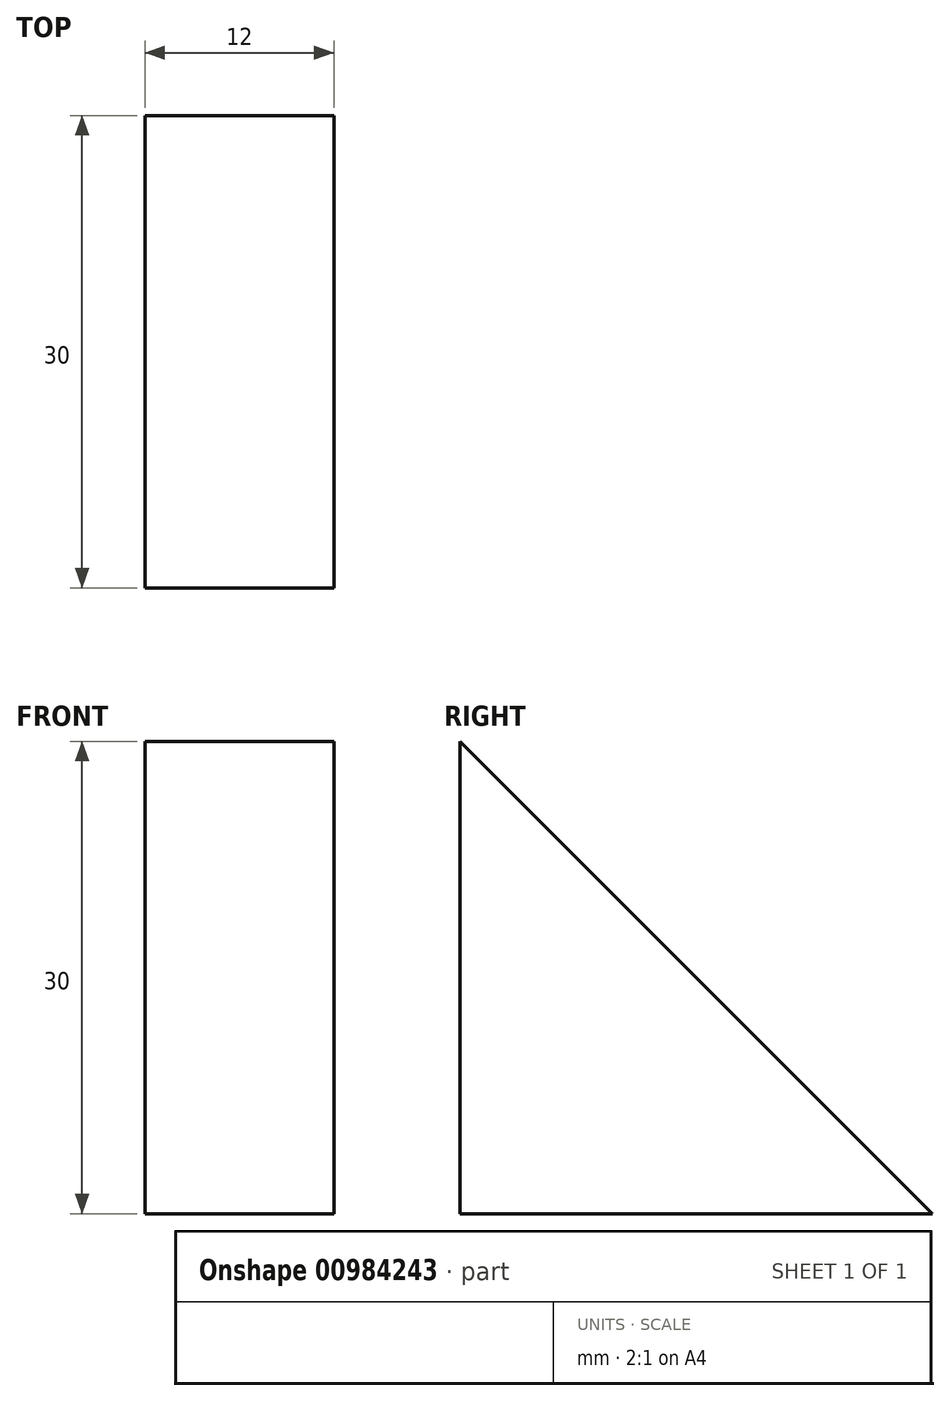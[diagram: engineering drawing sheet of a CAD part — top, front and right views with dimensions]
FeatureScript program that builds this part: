
annotation { "Feature Type Name" : "Feature", "Feature Type Description" : "" }
export const myFeature = defineFeature(function(context is Context, id is Id, definition is map)
    precondition{}
    {
        {
            var Q0;
            Q0=qCreatedBy(makeId("Right.planeOp"),FACE);
            var sketch = newSketch(context, id + "F0", { "sketchPlane" : qUnion([Q0])});
            skLineSegment(sketch, "E0", {"start": v(0, 30) * mm, "end": v(30, 0) * mm});
            skLineSegment(sketch, "E1", {"start": v(30, 0) * mm, "end": v(0, 0) * mm});
            skLineSegment(sketch, "E2", {"start": v(0, 0) * mm, "end": v(0, 30) * mm});
            skSolve(sketch);
        }
        {
            var Q0;
            Q0=makeQuery(id+"F0.imprint","IMPRINT",FACE,{"disambiguationData":[TD([[makeQuery(id+"F0.imprint","IMPRINT",EDGE,{"derivedFrom":sQuery(id+"F0.wireOp",EDGE,"E0")}),-1.0]])]});
            extrude(context, id + "F1", {"entities" : qUnion([Q0]), "oppositeDirection" : true, "depth" : 12 * mm, "offsetDistance" : 25 * mm});
        }
    });
